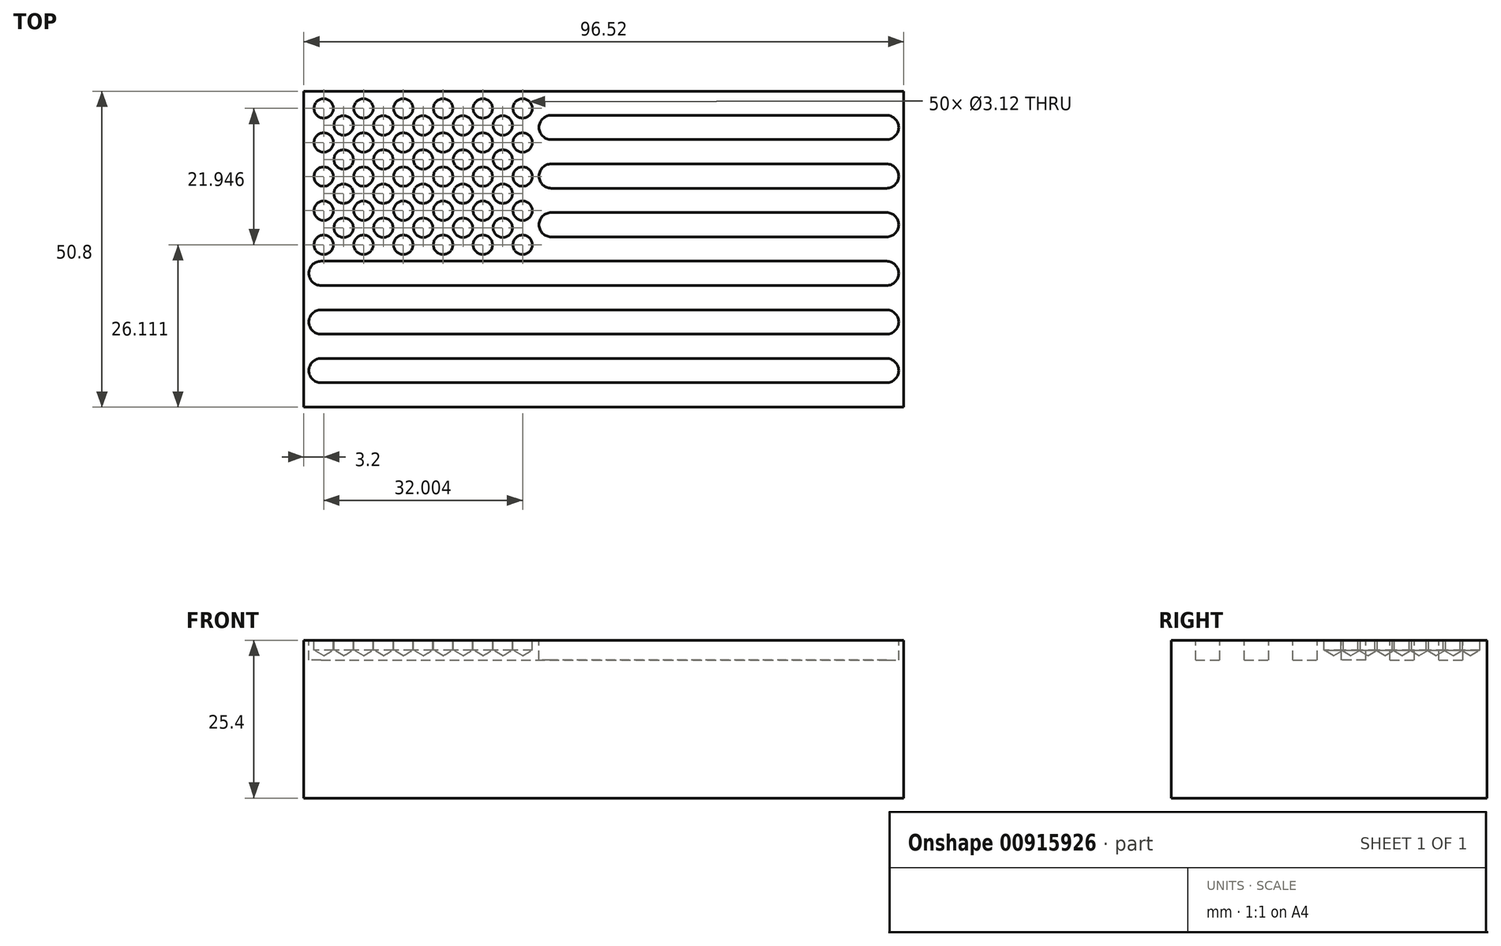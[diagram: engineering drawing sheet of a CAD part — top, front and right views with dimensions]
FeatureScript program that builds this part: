
annotation { "Feature Type Name" : "Feature", "Feature Type Description" : "" }
export const myFeature = defineFeature(function(context is Context, id is Id, definition is map)
    precondition{}
    {
        {
            var Q0;
            Q0=qCreatedBy(makeId("Top.planeOp"),FACE);
            var sketch = newSketch(context, id + "F0", { "sketchPlane" : qUnion([Q0])});
            skLineSegment(sketch, "E0.bottom", {"start": v(0, 0) * mm, "end": v(96.52, 0) * mm});
            skLineSegment(sketch, "E0.top", {"start": v(0, 50.8) * mm, "end": v(96.52, 50.8) * mm});
            skLineSegment(sketch, "E0.left", {"start": v(0, 0) * mm, "end": v(0, 50.8) * mm});
            skLineSegment(sketch, "E0.right", {"start": v(96.52, 0) * mm, "end": v(96.52, 50.8) * mm});
            skSolve(sketch);
        }
        {
            var Q0;
            Q0=makeQuery(id+"F0.imprint","IMPRINT",FACE,{"disambiguationData":[TD([[makeQuery(id+"F0.imprint","IMPRINT",EDGE,{"derivedFrom":sQuery(id+"F0.wireOp",EDGE,"E0.bottom")}),1.0]])]});
            extrude(context, id + "F1", {"entities" : qUnion([Q0]), "depth" : 25.4 * mm, "offsetDistance" : 25.4 * mm});
        }
        {
            var Q0;
            Q0=makeQuery(id+"F1.opExtrude","CAP_FACE",FACE,{"disambiguationData":[OSD([sQuery(id+"F0.wireOp",EDGE,"E0.bottom"),sQuery(id+"F0.wireOp",EDGE,"E0.top"),sQuery(id+"F0.wireOp",EDGE,"E0.left"),sQuery(id+"F0.wireOp",EDGE,"E0.right")])],"isStart":false});
            var sketch = newSketch(context, id + "F2", { "sketchPlane" : qUnion([Q0])});
            skPoint(sketch, "E1", {"position": v(3.2, 48.06) * mm});
            skPoint(sketch, "E2", {"position": v(9.6, 48.06) * mm});
            skPoint(sketch, "E3", {"position": v(16, 48.06) * mm});
            skPoint(sketch, "E4", {"position": v(22.4, 48.06) * mm});
            skPoint(sketch, "E5", {"position": v(28.8, 48.06) * mm});
            skPoint(sketch, "E6", {"position": v(35.2, 48.06) * mm});
            skPoint(sketch, "E7.1.0.0", {"position": v(35.2, 42.57) * mm});
            skPoint(sketch, "E7.1.0.1", {"position": v(16, 42.57) * mm});
            skPoint(sketch, "E7.1.0.2", {"position": v(28.8, 42.57) * mm});
            skPoint(sketch, "E7.1.0.3", {"position": v(3.2, 42.57) * mm});
            skPoint(sketch, "E7.1.0.4", {"position": v(22.4, 42.57) * mm});
            skPoint(sketch, "E7.1.0.5", {"position": v(9.6, 42.57) * mm});
            skPoint(sketch, "E7.2.0.0", {"position": v(35.2, 37.08) * mm});
            skPoint(sketch, "E7.2.0.1", {"position": v(16, 37.08) * mm});
            skPoint(sketch, "E7.2.0.2", {"position": v(28.8, 37.08) * mm});
            skPoint(sketch, "E7.2.0.3", {"position": v(3.2, 37.08) * mm});
            skPoint(sketch, "E7.2.0.4", {"position": v(22.4, 37.08) * mm});
            skPoint(sketch, "E7.2.0.5", {"position": v(9.6, 37.08) * mm});
            skPoint(sketch, "E7.3.0.0", {"position": v(35.2, 31.6) * mm});
            skPoint(sketch, "E7.3.0.1", {"position": v(16, 31.6) * mm});
            skPoint(sketch, "E7.3.0.2", {"position": v(28.8, 31.6) * mm});
            skPoint(sketch, "E7.3.0.3", {"position": v(3.2, 31.6) * mm});
            skPoint(sketch, "E7.3.0.4", {"position": v(22.4, 31.6) * mm});
            skPoint(sketch, "E7.3.0.5", {"position": v(9.6, 31.6) * mm});
            skPoint(sketch, "E7.4.0.0", {"position": v(35.2, 26.11) * mm});
            skPoint(sketch, "E7.4.0.1", {"position": v(16, 26.11) * mm});
            skPoint(sketch, "E7.4.0.2", {"position": v(28.8, 26.11) * mm});
            skPoint(sketch, "E7.4.0.3", {"position": v(3.2, 26.11) * mm});
            skPoint(sketch, "E7.4.0.4", {"position": v(22.4, 26.11) * mm});
            skPoint(sketch, "E7.4.0.5", {"position": v(9.6, 26.11) * mm});
            skLineSegment(sketch, "E7.direction1", {"start": v(3.2, 48.06) * mm, "end": v(3.2, 42.57) * mm, "construction": true});
            skPoint(sketch, "E8", {"position": v(6.4, 45.31) * mm});
            skPoint(sketch, "E9", {"position": v(6.4, 39.83) * mm});
            skPoint(sketch, "E10", {"position": v(6.4, 34.34) * mm});
            skPoint(sketch, "E11", {"position": v(6.4, 28.85) * mm});
            skPoint(sketch, "E12.1.0.0", {"position": v(12.8, 39.83) * mm});
            skPoint(sketch, "E12.1.0.1", {"position": v(12.8, 34.34) * mm});
            skPoint(sketch, "E12.1.0.2", {"position": v(12.8, 45.31) * mm});
            skPoint(sketch, "E12.1.0.3", {"position": v(12.8, 28.85) * mm});
            skPoint(sketch, "E12.2.0.0", {"position": v(19.2, 39.83) * mm});
            skPoint(sketch, "E12.2.0.1", {"position": v(19.2, 34.34) * mm});
            skPoint(sketch, "E12.2.0.2", {"position": v(19.2, 45.31) * mm});
            skPoint(sketch, "E12.2.0.3", {"position": v(19.2, 28.85) * mm});
            skPoint(sketch, "E12.3.0.0", {"position": v(25.6, 39.83) * mm});
            skPoint(sketch, "E12.3.0.1", {"position": v(25.6, 34.34) * mm});
            skPoint(sketch, "E12.3.0.2", {"position": v(25.6, 45.31) * mm});
            skPoint(sketch, "E12.3.0.3", {"position": v(25.6, 28.85) * mm});
            skPoint(sketch, "E12.4.0.0", {"position": v(32, 39.83) * mm});
            skPoint(sketch, "E12.4.0.1", {"position": v(32, 34.34) * mm});
            skPoint(sketch, "E12.4.0.2", {"position": v(32, 45.31) * mm});
            skPoint(sketch, "E12.4.0.3", {"position": v(32, 28.85) * mm});
            skLineSegment(sketch, "E12.direction1", {"start": v(6.4, 28.85) * mm, "end": v(12.8, 28.85) * mm, "construction": true});
            skCircle(sketch, "E13", {"center": v(35.2, 48.06) * mm, "radius": 1.56 * mm});
            skSolve(sketch);
        }
        {
            var Q0;
            Q0=sQuery(id+"F2.wireOp",VERTEX,"E5");
            var Q1;
            Q1=sQuery(id+"F2.wireOp",VERTEX,"E13.center");
            var Q2;
            Q2=sQuery(id+"F2.wireOp",VERTEX,"E4");
            var Q3;
            Q3=sQuery(id+"F2.wireOp",VERTEX,"E3");
            var Q4;
            Q4=sQuery(id+"F2.wireOp",VERTEX,"E2");
            var Q5;
            Q5=sQuery(id+"F2.wireOp",VERTEX,"E1");
            var Q6;
            Q6=sQuery(id+"F2.wireOp",VERTEX,"E8");
            var Q7;
            Q7=sQuery(id+"F2.wireOp",VERTEX,"E7.1.0.5");
            var Q8;
            Q8=sQuery(id+"F2.wireOp",VERTEX,"E12.1.0.2");
            var Q9;
            Q9=sQuery(id+"F2.wireOp",VERTEX,"E7.1.0.1");
            var Q10;
            Q10=sQuery(id+"F2.wireOp",VERTEX,"E12.2.0.2");
            var Q11;
            Q11=sQuery(id+"F2.wireOp",VERTEX,"E7.1.0.4");
            var Q12;
            Q12=sQuery(id+"F2.wireOp",VERTEX,"E12.3.0.2");
            var Q13;
            Q13=sQuery(id+"F2.wireOp",VERTEX,"E7.1.0.2");
            var Q14;
            Q14=sQuery(id+"F2.wireOp",VERTEX,"E12.4.0.2");
            var Q15;
            Q15=sQuery(id+"F2.wireOp",VERTEX,"E7.1.0.0");
            var Q16;
            Q16=sQuery(id+"F2.wireOp",VERTEX,"E12.4.0.0");
            var Q17;
            Q17=sQuery(id+"F2.wireOp",VERTEX,"E7.2.0.0");
            var Q18;
            Q18=sQuery(id+"F2.wireOp",VERTEX,"E12.4.0.1");
            var Q19;
            Q19=sQuery(id+"F2.wireOp",VERTEX,"E7.2.0.2");
            var Q20;
            Q20=sQuery(id+"F2.wireOp",VERTEX,"E12.3.0.0");
            var Q21;
            Q21=sQuery(id+"F2.wireOp",VERTEX,"E12.2.0.0");
            var Q22;
            Q22=sQuery(id+"F2.wireOp",VERTEX,"E7.2.0.4");
            var Q23;
            Q23=sQuery(id+"F2.wireOp",VERTEX,"E12.3.0.1");
            var Q24;
            Q24=sQuery(id+"F2.wireOp",VERTEX,"E7.3.0.2");
            var Q25;
            Q25=sQuery(id+"F2.wireOp",VERTEX,"E12.4.0.3");
            var Q26;
            Q26=sQuery(id+"F2.wireOp",VERTEX,"E7.3.0.0");
            var Q27;
            Q27=sQuery(id+"F2.wireOp",VERTEX,"E7.4.0.2");
            var Q28;
            Q28=sQuery(id+"F2.wireOp",VERTEX,"E12.3.0.3");
            var Q29;
            Q29=sQuery(id+"F2.wireOp",VERTEX,"E7.3.0.4");
            var Q30;
            Q30=sQuery(id+"F2.wireOp",VERTEX,"E12.2.0.1");
            var Q31;
            Q31=sQuery(id+"F2.wireOp",VERTEX,"E12.1.0.0");
            var Q32;
            Q32=sQuery(id+"F2.wireOp",VERTEX,"E7.direction1.end");
            var Q33;
            Q33=sQuery(id+"F2.wireOp",VERTEX,"E9");
            var Q34;
            Q34=sQuery(id+"F2.wireOp",VERTEX,"E7.2.0.3");
            var Q35;
            Q35=sQuery(id+"F2.wireOp",VERTEX,"E10");
            var Q36;
            Q36=sQuery(id+"F2.wireOp",VERTEX,"E7.2.0.5");
            var Q37;
            Q37=sQuery(id+"F2.wireOp",VERTEX,"E12.1.0.1");
            var Q38;
            Q38=sQuery(id+"F2.wireOp",VERTEX,"E7.3.0.5");
            var Q39;
            Q39=sQuery(id+"F2.wireOp",VERTEX,"E11");
            var Q40;
            Q40=sQuery(id+"F2.wireOp",VERTEX,"E7.3.0.3");
            var Q41;
            Q41=sQuery(id+"F2.wireOp",VERTEX,"E7.4.0.3");
            var Q42;
            Q42=sQuery(id+"F2.wireOp",VERTEX,"E7.4.0.1");
            var Q43;
            Q43=sQuery(id+"F2.wireOp",VERTEX,"E12.2.0.3");
            var Q44;
            Q44=sQuery(id+"F2.wireOp",VERTEX,"E7.4.0.4");
            var Q45;
            Q45=sQuery(id+"F2.wireOp",VERTEX,"E7.4.0.0");
            var Q46;
            Q46=sQuery(id+"F2.wireOp",VERTEX,"E7.3.0.1");
            var Q47;
            Q47=sQuery(id+"F2.wireOp",VERTEX,"E7.4.0.5");
            var Q48;
            Q48=sQuery(id+"F2.wireOp",VERTEX,"E12.direction1.end");
            var Q49;
            Q49=sQuery(id+"F2.wireOp",VERTEX,"E7.2.0.1");
            var Q50;
            Q50=makeQuery(id+"F1.opExtrude","SWEPT_BODY",BODY,{"disambiguationData":[OSD([sQuery(id+"F0.wireOp",EDGE,"E0.bottom"),sQuery(id+"F0.wireOp",EDGE,"E0.top"),sQuery(id+"F0.wireOp",EDGE,"E0.left"),sQuery(id+"F0.wireOp",EDGE,"E0.right")])]});
            hole(context, id + "F3", {"style" : HoleStyle.SIMPLE, "endStyle" : HoleEndStyle.BLIND, "holeDiameter" : 3.12 * mm, "majorDiameter" : 6.35 * mm, "holeDepth" : 1.59 * mm, "isTappedThrough" : true, "tappedDepth" : 12.7 * mm, "tapClearance" : 3, "startFromSketch" : true, "locations" : qUnion([Q0, Q1, Q2, Q3, Q4, Q5, Q6, Q7, Q8, Q9, Q10, Q11, Q12, Q13, Q14, Q15, Q16, Q17, Q18, Q19, Q20, Q21, Q22, Q23, Q24, Q25, Q26, Q27, Q28, Q29, Q30, Q31, Q32, Q33, Q34, Q35, Q36, Q37, Q38, Q39, Q40, Q41, Q42, Q43, Q44, Q45, Q46, Q47, Q48, Q49]), "scope" : qUnion([Q50])});
        }
        {
            var Q0;
            Q0=makeQuery(id+"F1.opExtrude","CAP_FACE",FACE,{"disambiguationData":[OSD([sQuery(id+"F0.wireOp",EDGE,"E0.bottom"),sQuery(id+"F0.wireOp",EDGE,"E0.top"),sQuery(id+"F0.wireOp",EDGE,"E0.left"),sQuery(id+"F0.wireOp",EDGE,"E0.right")])],"isStart":false});
            var sketch = newSketch(context, id + "F4", { "sketchPlane" : qUnion([Q0])});
            skLineSegment(sketch, "E14.bottom", {"start": v(2.77, 3.91) * mm, "end": v(93.75, 3.91) * mm});
            skLineSegment(sketch, "E14.top", {"start": v(2.77, 7.82) * mm, "end": v(93.75, 7.82) * mm});
            skLineSegment(sketch, "E14.left", {"start": v(2.77, 3.91) * mm, "end": v(2.77, 7.82) * mm});
            skLineSegment(sketch, "E14.right", {"start": v(93.75, 3.91) * mm, "end": v(93.75, 7.82) * mm});
            skLineSegment(sketch, "E15.bottom", {"start": v(2.77, 15.65) * mm, "end": v(93.75, 15.65) * mm});
            skLineSegment(sketch, "E15.top", {"start": v(2.77, 11.73) * mm, "end": v(93.75, 11.73) * mm});
            skLineSegment(sketch, "E15.left", {"start": v(2.77, 15.65) * mm, "end": v(2.77, 11.73) * mm});
            skLineSegment(sketch, "E15.right", {"start": v(93.75, 15.65) * mm, "end": v(93.75, 11.73) * mm});
            skLineSegment(sketch, "E16.bottom", {"start": v(2.77, 19.56) * mm, "end": v(93.75, 19.56) * mm});
            skLineSegment(sketch, "E16.top", {"start": v(2.77, 23.47) * mm, "end": v(93.75, 23.47) * mm});
            skLineSegment(sketch, "E16.left", {"start": v(2.77, 19.56) * mm, "end": v(2.77, 23.47) * mm});
            skLineSegment(sketch, "E16.right", {"start": v(93.75, 19.56) * mm, "end": v(93.75, 23.47) * mm});
            skLineSegment(sketch, "E17.bottom", {"start": v(93.75, 27.38) * mm, "end": v(39.8, 27.38) * mm});
            skLineSegment(sketch, "E17.top", {"start": v(93.75, 31.3) * mm, "end": v(39.8, 31.3) * mm});
            skLineSegment(sketch, "E17.left", {"start": v(93.75, 27.38) * mm, "end": v(93.75, 31.3) * mm});
            skLineSegment(sketch, "E17.right", {"start": v(39.8, 27.38) * mm, "end": v(39.8, 31.3) * mm});
            skLineSegment(sketch, "E18.bottom", {"start": v(93.75, 35.2) * mm, "end": v(39.8, 35.2) * mm});
            skLineSegment(sketch, "E18.top", {"start": v(93.75, 39.12) * mm, "end": v(39.8, 39.12) * mm});
            skLineSegment(sketch, "E18.left", {"start": v(93.75, 35.2) * mm, "end": v(93.75, 39.12) * mm});
            skLineSegment(sketch, "E18.right", {"start": v(39.8, 35.2) * mm, "end": v(39.8, 39.12) * mm});
            skLineSegment(sketch, "E19.bottom", {"start": v(93.75, 43.03) * mm, "end": v(39.8, 43.03) * mm});
            skLineSegment(sketch, "E19.top", {"start": v(93.75, 46.94) * mm, "end": v(39.8, 46.94) * mm});
            skLineSegment(sketch, "E19.left", {"start": v(93.75, 43.03) * mm, "end": v(93.75, 46.94) * mm});
            skLineSegment(sketch, "E19.right", {"start": v(39.8, 43.03) * mm, "end": v(39.8, 46.94) * mm});
            skArc(sketch, "E20", {"start": v(93.75, 43.03) * mm, "mid": v(95.7, 44.98) * mm, "end": v(93.75, 46.94) * mm});
            skArc(sketch, "E21", {"start": v(93.75, 35.2) * mm, "mid": v(95.7, 37.16) * mm, "end": v(93.75, 39.12) * mm});
            skArc(sketch, "E22", {"start": v(93.75, 27.38) * mm, "mid": v(95.7, 29.34) * mm, "end": v(93.75, 31.3) * mm});
            skArc(sketch, "E23", {"start": v(93.75, 19.56) * mm, "mid": v(95.7, 21.51) * mm, "end": v(93.75, 23.47) * mm});
            skArc(sketch, "E24", {"start": v(93.75, 11.73) * mm, "mid": v(95.7, 13.7) * mm, "end": v(93.75, 15.65) * mm});
            skArc(sketch, "E25", {"start": v(93.75, 3.91) * mm, "mid": v(95.7, 5.87) * mm, "end": v(93.75, 7.82) * mm});
            skArc(sketch, "E26", {"start": v(39.8, 46.94) * mm, "mid": v(37.85, 44.98) * mm, "end": v(39.8, 43.03) * mm});
            skArc(sketch, "E27", {"start": v(39.8, 39.12) * mm, "mid": v(37.85, 37.16) * mm, "end": v(39.8, 35.2) * mm});
            skArc(sketch, "E28", {"start": v(39.8, 31.3) * mm, "mid": v(37.85, 29.34) * mm, "end": v(39.8, 27.38) * mm});
            skArc(sketch, "E29", {"start": v(2.77, 23.47) * mm, "mid": v(0.81, 21.51) * mm, "end": v(2.77, 19.56) * mm});
            skArc(sketch, "E30", {"start": v(2.77, 15.65) * mm, "mid": v(0.81, 13.7) * mm, "end": v(2.77, 11.73) * mm});
            skArc(sketch, "E31", {"start": v(2.77, 7.82) * mm, "mid": v(0.81, 5.87) * mm, "end": v(2.77, 3.91) * mm});
            skSolve(sketch);
        }
        {
            var Q0;
            Q0=makeQuery(id+"F4.imprint","IMPRINT",FACE,{"disambiguationData":[TD([[makeQuery(id+"F4.imprint","IMPRINT",EDGE,{"derivedFrom":sQuery(id+"F4.wireOp",EDGE,"E19.right")}),1.0]])]});
            var Q1;
            Q1=makeQuery(id+"F4.imprint","IMPRINT",FACE,{"disambiguationData":[TD([[makeQuery(id+"F4.imprint","IMPRINT",EDGE,{"derivedFrom":sQuery(id+"F4.wireOp",EDGE,"E19.bottom")}),-1.0]])]});
            var Q2;
            Q2=makeQuery(id+"F4.imprint","IMPRINT",FACE,{"disambiguationData":[TD([[makeQuery(id+"F4.imprint","IMPRINT",EDGE,{"derivedFrom":sQuery(id+"F4.wireOp",EDGE,"E19.left")}),-1.0]])]});
            var Q3;
            Q3=makeQuery(id+"F4.imprint","IMPRINT",FACE,{"disambiguationData":[TD([[makeQuery(id+"F4.imprint","IMPRINT",EDGE,{"derivedFrom":sQuery(id+"F4.wireOp",EDGE,"E18.left")}),-1.0]])]});
            var Q4;
            Q4=makeQuery(id+"F4.imprint","IMPRINT",FACE,{"disambiguationData":[TD([[makeQuery(id+"F4.imprint","IMPRINT",EDGE,{"derivedFrom":sQuery(id+"F4.wireOp",EDGE,"E18.bottom")}),-1.0]])]});
            var Q5;
            Q5=makeQuery(id+"F4.imprint","IMPRINT",FACE,{"disambiguationData":[TD([[makeQuery(id+"F4.imprint","IMPRINT",EDGE,{"derivedFrom":sQuery(id+"F4.wireOp",EDGE,"E18.right")}),1.0]])]});
            var Q6;
            Q6=makeQuery(id+"F4.imprint","IMPRINT",FACE,{"disambiguationData":[TD([[makeQuery(id+"F4.imprint","IMPRINT",EDGE,{"derivedFrom":sQuery(id+"F4.wireOp",EDGE,"E17.right")}),1.0]])]});
            var Q7;
            Q7=makeQuery(id+"F4.imprint","IMPRINT",FACE,{"disambiguationData":[TD([[makeQuery(id+"F4.imprint","IMPRINT",EDGE,{"derivedFrom":sQuery(id+"F4.wireOp",EDGE,"E17.bottom")}),-1.0]])]});
            var Q8;
            Q8=makeQuery(id+"F4.imprint","IMPRINT",FACE,{"disambiguationData":[TD([[makeQuery(id+"F4.imprint","IMPRINT",EDGE,{"derivedFrom":sQuery(id+"F4.wireOp",EDGE,"E17.left")}),-1.0]])]});
            var Q9;
            Q9=makeQuery(id+"F4.imprint","IMPRINT",FACE,{"disambiguationData":[TD([[makeQuery(id+"F4.imprint","IMPRINT",EDGE,{"derivedFrom":sQuery(id+"F4.wireOp",EDGE,"E16.right")}),-1.0]])]});
            var Q10;
            Q10=makeQuery(id+"F4.imprint","IMPRINT",FACE,{"disambiguationData":[TD([[makeQuery(id+"F4.imprint","IMPRINT",EDGE,{"derivedFrom":sQuery(id+"F4.wireOp",EDGE,"E16.bottom")}),1.0]])]});
            var Q11;
            Q11=makeQuery(id+"F4.imprint","IMPRINT",FACE,{"disambiguationData":[TD([[makeQuery(id+"F4.imprint","IMPRINT",EDGE,{"derivedFrom":sQuery(id+"F4.wireOp",EDGE,"E15.right")}),1.0]])]});
            var Q12;
            Q12=makeQuery(id+"F4.imprint","IMPRINT",FACE,{"disambiguationData":[TD([[makeQuery(id+"F4.imprint","IMPRINT",EDGE,{"derivedFrom":sQuery(id+"F4.wireOp",EDGE,"E15.bottom")}),-1.0]])]});
            var Q13;
            Q13=makeQuery(id+"F4.imprint","IMPRINT",FACE,{"disambiguationData":[TD([[makeQuery(id+"F4.imprint","IMPRINT",EDGE,{"derivedFrom":sQuery(id+"F4.wireOp",EDGE,"E14.right")}),-1.0]])]});
            var Q14;
            Q14=makeQuery(id+"F4.imprint","IMPRINT",FACE,{"disambiguationData":[TD([[makeQuery(id+"F4.imprint","IMPRINT",EDGE,{"derivedFrom":sQuery(id+"F4.wireOp",EDGE,"E14.bottom")}),1.0]])]});
            var Q15;
            Q15=makeQuery(id+"F4.imprint","IMPRINT",FACE,{"disambiguationData":[TD([[makeQuery(id+"F4.imprint","IMPRINT",EDGE,{"derivedFrom":sQuery(id+"F4.wireOp",EDGE,"E14.left")}),1.0]])]});
            var Q16;
            Q16=makeQuery(id+"F4.imprint","IMPRINT",FACE,{"disambiguationData":[TD([[makeQuery(id+"F4.imprint","IMPRINT",EDGE,{"derivedFrom":sQuery(id+"F4.wireOp",EDGE,"E15.left")}),-1.0]])]});
            var Q17;
            Q17=makeQuery(id+"F4.imprint","IMPRINT",FACE,{"disambiguationData":[TD([[makeQuery(id+"F4.imprint","IMPRINT",EDGE,{"derivedFrom":sQuery(id+"F4.wireOp",EDGE,"E16.left")}),1.0]])]});
            extrude(context, id + "F5", {"entities" : qUnion([Q0, Q1, Q2, Q3, Q4, Q5, Q6, Q7, Q8, Q9, Q10, Q11, Q12, Q13, Q14, Q15, Q16, Q17]), "operationType" : NewBodyOperationType.REMOVE, "oppositeDirection" : true, "depth" : 3.17 * mm, "offsetDistance" : 25.4 * mm});
        }
    });
